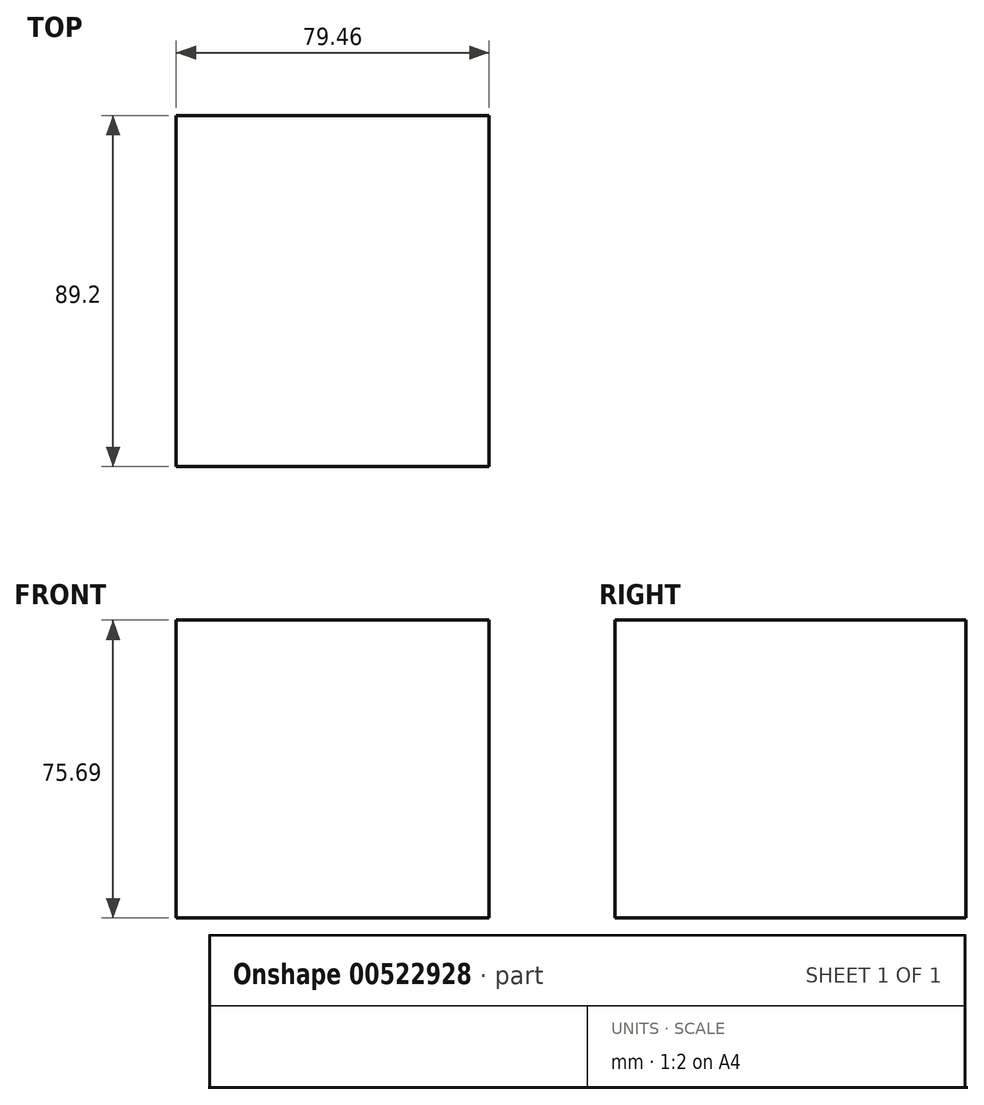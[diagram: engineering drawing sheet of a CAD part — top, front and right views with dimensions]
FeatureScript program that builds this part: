
annotation { "Feature Type Name" : "Feature", "Feature Type Description" : "" }
export const myFeature = defineFeature(function(context is Context, id is Id, definition is map)
    precondition{}
    {
        {
            var Q0;
            Q0=qCreatedBy(makeId("Top.planeOp"),FACE);
            var sketch = newSketch(context, id + "F0", { "sketchPlane" : qUnion([Q0])});
            skLineSegment(sketch, "E0.bottom", {"start": v(-53.22, -59.61) * mm, "end": v(26.24, -59.61) * mm});
            skLineSegment(sketch, "E0.top", {"start": v(-53.22, 29.6) * mm, "end": v(26.24, 29.6) * mm});
            skLineSegment(sketch, "E0.left", {"start": v(-53.22, -59.61) * mm, "end": v(-53.22, 29.6) * mm});
            skLineSegment(sketch, "E0.right", {"start": v(26.24, -59.61) * mm, "end": v(26.24, 29.6) * mm});
            skSolve(sketch);
        }
        {
            var Q0;
            Q0=makeQuery(id+"F0.imprint","IMPRINT",FACE,{"disambiguationData":[TD([[makeQuery(id+"F0.imprint","IMPRINT",EDGE,{"derivedFrom":sQuery(id+"F0.wireOp",EDGE,"E0.bottom")}),1.0]])]});
            extrude(context, id + "F1", {"entities" : qUnion([Q0]), "depth" : 75.7 * mm, "offsetDistance" : 25.4 * mm});
        }
    });
